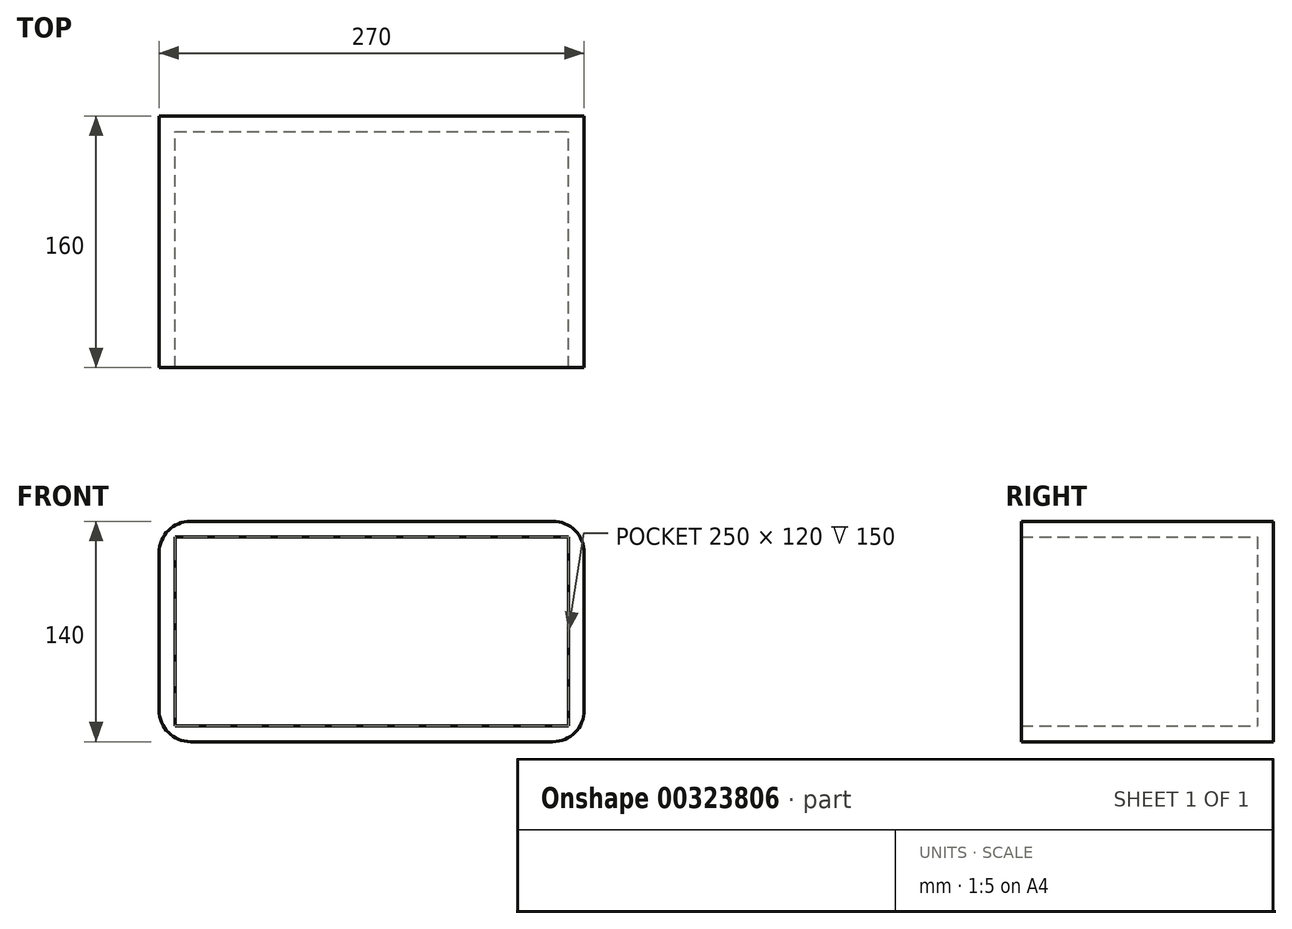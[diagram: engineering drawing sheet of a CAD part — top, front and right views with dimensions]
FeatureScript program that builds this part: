
annotation { "Feature Type Name" : "Feature", "Feature Type Description" : "" }
export const myFeature = defineFeature(function(context is Context, id is Id, definition is map)
    precondition{}
    {
        {
            var Q0;
            Q0=qCreatedBy(makeId("Front.planeOp"),FACE);
            var sketch = newSketch(context, id + "F0", { "sketchPlane" : qUnion([Q0])});
            skLineSegment(sketch, "E0.bottom", {"start": v(-135, 70) * mm, "end": v(135, 70) * mm});
            skLineSegment(sketch, "E0.top", {"start": v(-135, -70) * mm, "end": v(135, -70) * mm});
            skLineSegment(sketch, "E0.left", {"start": v(-135, 70) * mm, "end": v(-135, -70) * mm});
            skLineSegment(sketch, "E0.right", {"start": v(135, 70) * mm, "end": v(135, -70) * mm});
            skPoint(sketch, "E0.middle", {"position": v(0, 0) * mm});
            skSolve(sketch);
        }
        {
            var Q0;
            Q0=makeQuery(id+"F0.imprint","IMPRINT",FACE,{"disambiguationData":[TD([[makeQuery(id+"F0.imprint","IMPRINT",EDGE,{"derivedFrom":sQuery(id+"F0.wireOp",EDGE,"E0.bottom")}),-1.0]])]});
            extrude(context, id + "F1", {"entities" : qUnion([Q0]), "depth" : 160 * mm});
        }
        {
            var Q0;
            Q0=makeQuery(id+"F1.opExtrude","CAP_FACE",FACE,{"disambiguationData":[OSD([sQuery(id+"F0.wireOp",EDGE,"E0.bottom"),sQuery(id+"F0.wireOp",EDGE,"E0.top"),sQuery(id+"F0.wireOp",EDGE,"E0.left"),sQuery(id+"F0.wireOp",EDGE,"E0.right")])],"isStart":false});
            shell(context, id + "F2", {"entities" : qUnion([Q0]), "thickness" : 10 * mm});
        }
        {
            var Q0;
            Q0=makeQuery(id+"F1.opExtrude","SWEPT_EDGE",EDGE,{"disambiguationData":[OSD([sQuery(id+"F0.wireOp",EDGE,"E0.bottom"),sQuery(id+"F0.wireOp",EDGE,"E0.left")])]});
            var Q1;
            Q1=makeQuery(id+"F1.opExtrude","SWEPT_EDGE",EDGE,{"disambiguationData":[OSD([sQuery(id+"F0.wireOp",EDGE,"E0.top"),sQuery(id+"F0.wireOp",EDGE,"E0.right")])]});
            var Q2;
            Q2=makeQuery(id+"F1.opExtrude","SWEPT_EDGE",EDGE,{"disambiguationData":[OSD([sQuery(id+"F0.wireOp",EDGE,"E0.bottom"),sQuery(id+"F0.wireOp",EDGE,"E0.right")])]});
            var Q3;
            Q3=makeQuery(id+"F1.opExtrude","SWEPT_EDGE",EDGE,{"disambiguationData":[OSD([sQuery(id+"F0.wireOp",EDGE,"E0.top"),sQuery(id+"F0.wireOp",EDGE,"E0.left")])]});
            fillet(context, id + "F3", {"entities" : qUnion([Q0, Q1, Q2, Q3]), "radius" : 20 * mm, "tangentPropagation" : true, "allowEdgeOverflow" : false});
        }
    });
